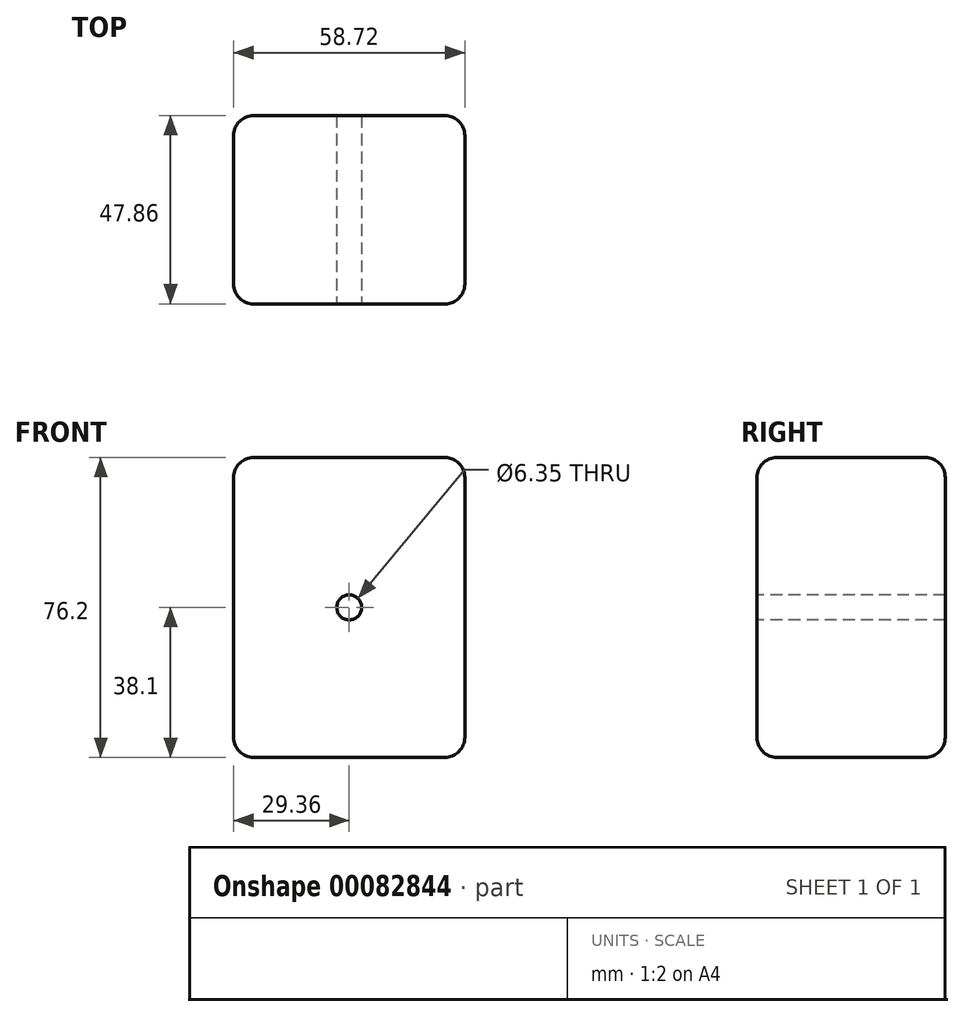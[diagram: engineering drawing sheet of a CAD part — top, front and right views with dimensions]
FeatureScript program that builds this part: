
annotation { "Feature Type Name" : "Feature", "Feature Type Description" : "" }
export const myFeature = defineFeature(function(context is Context, id is Id, definition is map)
    precondition{}
    {
        {
            var Q0;
            Q0=qCreatedBy(makeId("Top.planeOp"),FACE);
            var sketch = newSketch(context, id + "F0", { "sketchPlane" : qUnion([Q0])});
            skLineSegment(sketch, "E0.bottom", {"start": v(-29.36, 23.93) * mm, "end": v(29.36, 23.93) * mm});
            skLineSegment(sketch, "E0.top", {"start": v(-29.36, -23.93) * mm, "end": v(29.36, -23.93) * mm});
            skLineSegment(sketch, "E0.left", {"start": v(-29.36, 23.93) * mm, "end": v(-29.36, -23.93) * mm});
            skLineSegment(sketch, "E0.right", {"start": v(29.36, 23.93) * mm, "end": v(29.36, -23.93) * mm});
            skPoint(sketch, "E0.middle", {"position": v(0, 0) * mm});
            skSolve(sketch);
        }
        {
            var Q0;
            Q0=makeQuery(id+"F0.imprint","IMPRINT",FACE,{"disambiguationData":[TD([[makeQuery(id+"F0.imprint","IMPRINT",EDGE,{"derivedFrom":sQuery(id+"F0.wireOp",EDGE,"E0.bottom")}),-1.0]])]});
            extrude(context, id + "F1", {"entities" : qUnion([Q0]), "depth" : 76.2 * mm});
        }
        {
            var Q0;
            Q0=makeQuery(id+"F1.opExtrude","SWEPT_EDGE",EDGE,{"disambiguationData":[OSD([sQuery(id+"F0.wireOp",EDGE,"E0.bottom"),sQuery(id+"F0.wireOp",EDGE,"E0.right")])]});
            var Q1;
            Q1=makeQuery(id+"F1.opExtrude","CAP_EDGE",EDGE,{"disambiguationData":[OSD([sQuery(id+"F0.wireOp",EDGE,"E0.bottom")])],"isStart":false});
            var Q2;
            Q2=makeQuery(id+"F1.opExtrude","SWEPT_EDGE",EDGE,{"disambiguationData":[OSD([sQuery(id+"F0.wireOp",EDGE,"E0.bottom"),sQuery(id+"F0.wireOp",EDGE,"E0.left")])]});
            var Q3;
            Q3=makeQuery(id+"F1.opExtrude","SWEPT_FACE",FACE,{"disambiguationData":[OSD([sQuery(id+"F0.wireOp",EDGE,"E0.bottom")])]});
            var Q4;
            Q4=makeQuery(id+"F1.opExtrude","CAP_EDGE",EDGE,{"disambiguationData":[OSD([sQuery(id+"F0.wireOp",EDGE,"E0.right")])],"isStart":false});
            var Q5;
            Q5=makeQuery(id+"F1.opExtrude","SWEPT_EDGE",EDGE,{"disambiguationData":[OSD([sQuery(id+"F0.wireOp",EDGE,"E0.top"),sQuery(id+"F0.wireOp",EDGE,"E0.right")])]});
            var Q6;
            Q6=makeQuery(id+"F1.opExtrude","SWEPT_FACE",FACE,{"disambiguationData":[OSD([sQuery(id+"F0.wireOp",EDGE,"E0.right")])]});
            var Q7;
            Q7=makeQuery(id+"F1.opExtrude","CAP_EDGE",EDGE,{"disambiguationData":[OSD([sQuery(id+"F0.wireOp",EDGE,"E0.left")])],"isStart":false});
            var Q8;
            Q8=makeQuery(id+"F1.opExtrude","SWEPT_EDGE",EDGE,{"disambiguationData":[OSD([sQuery(id+"F0.wireOp",EDGE,"E0.top"),sQuery(id+"F0.wireOp",EDGE,"E0.left")])]});
            var Q9;
            Q9=makeQuery(id+"F1.opExtrude","SWEPT_FACE",FACE,{"disambiguationData":[OSD([sQuery(id+"F0.wireOp",EDGE,"E0.left")])]});
            fillet(context, id + "F2", {"entities" : qUnion([Q0, Q1, Q2, Q3, Q4, Q5, Q6, Q7, Q8, Q9]), "radius" : 5.08 * mm, "tangentPropagation" : true, "allowEdgeOverflow" : false});
        }
        {
            var Q0;
            Q0=makeQuery(id+"F1.opExtrude","SWEPT_FACE",FACE,{"disambiguationData":[OSD([sQuery(id+"F0.wireOp",EDGE,"E0.top")])]});
            var Q1;
            Q1=makeQuery(id+"F1.opExtrude","CAP_EDGE",EDGE,{"disambiguationData":[OSD([sQuery(id+"F0.wireOp",EDGE,"E0.top")])],"isStart":false});
            fillet(context, id + "F3", {"entities" : qUnion([Q0, Q1]), "radius" : 5.08 * mm, "tangentPropagation" : true, "allowEdgeOverflow" : false});
        }
        {
            var Q0;
            Q0=makeQuery(id+"F1.opExtrude","SWEPT_FACE",FACE,{"disambiguationData":[OSD([sQuery(id+"F0.wireOp",EDGE,"E0.top")])]});
            var sketch = newSketch(context, id + "F4", { "sketchPlane" : qUnion([Q0])});
            skCircle(sketch, "E1", {"center": v(0, 38.1) * mm, "radius": 13.32 * mm});
            skPoint(sketch, "E1.centerSnap0", {"position": v(-24.28, 38.1) * mm});
            skSolve(sketch);
        }
        {
            var Q0;
            Q0=sQuery(id+"F4.wireOp",VERTEX,"E1.center");
            var Q1;
            Q1=makeQuery(id+"F1.opExtrude","SWEPT_BODY",BODY,{"disambiguationData":[OSD([sQuery(id+"F0.wireOp",EDGE,"E0.bottom"),sQuery(id+"F0.wireOp",EDGE,"E0.top"),sQuery(id+"F0.wireOp",EDGE,"E0.left"),sQuery(id+"F0.wireOp",EDGE,"E0.right")])]});
            hole(context, id + "F5", {"style" : HoleStyle.SIMPLE, "endStyle" : HoleEndStyle.THROUGH, "holeDiameter" : 6.35 * mm, "locations" : qUnion([Q0]), "scope" : qUnion([Q1]), "isTappedThrough" : true});
        }
    });
